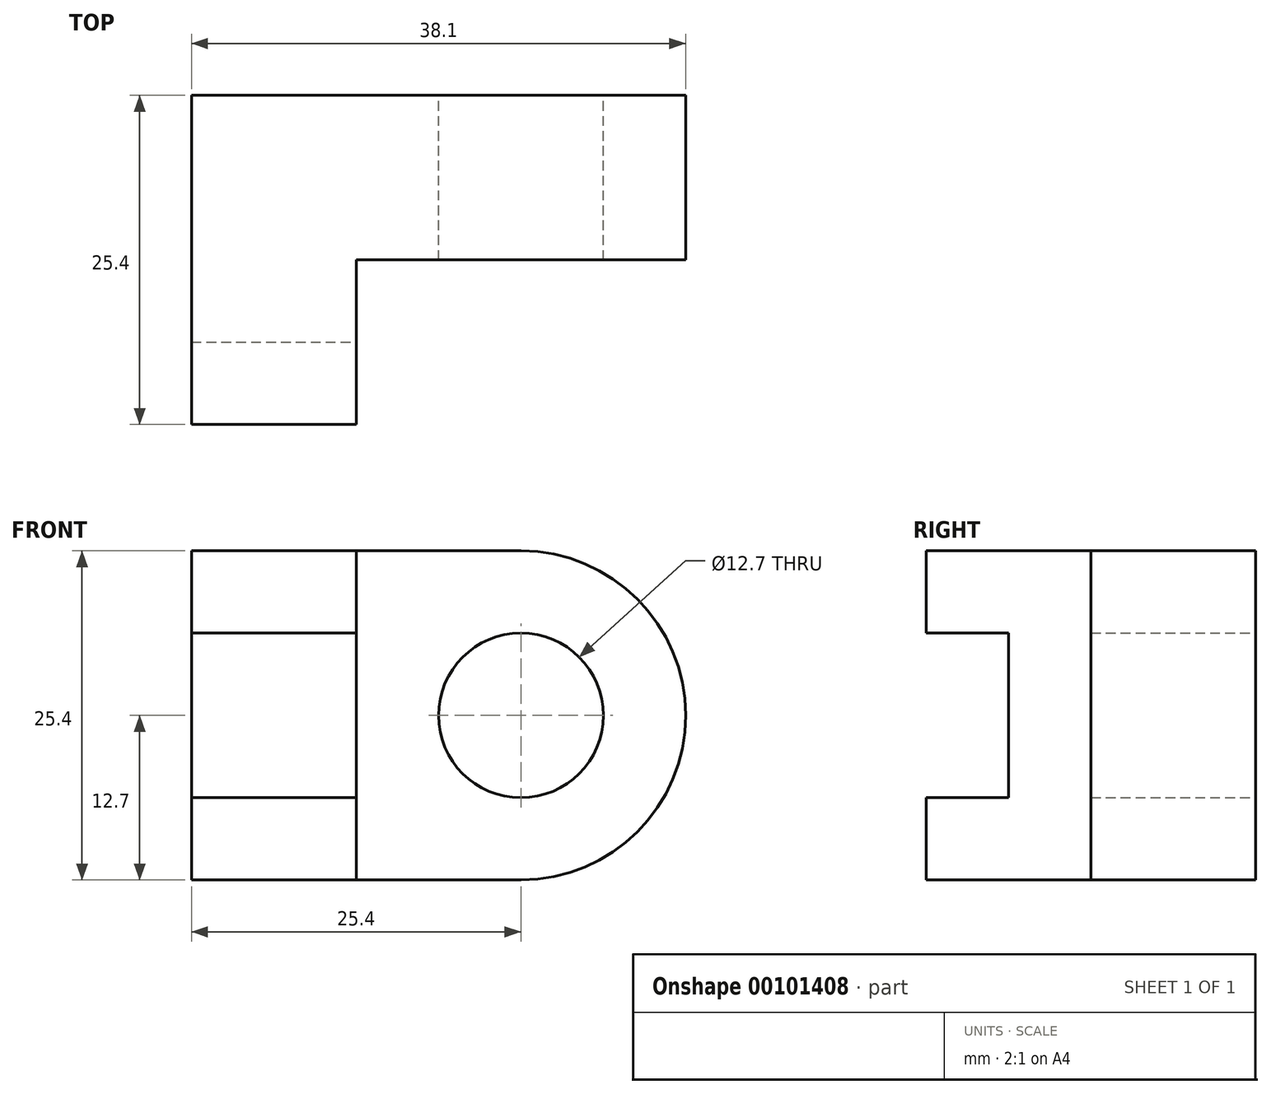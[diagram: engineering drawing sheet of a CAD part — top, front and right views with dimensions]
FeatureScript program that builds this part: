
annotation { "Feature Type Name" : "Feature", "Feature Type Description" : "" }
export const myFeature = defineFeature(function(context is Context, id is Id, definition is map)
    precondition{}
    {
        {
            var Q0;
            Q0=qCreatedBy(makeId("Front.planeOp"),FACE);
            var sketch = newSketch(context, id + "F0", { "sketchPlane" : qUnion([Q0])});
            skLineSegment(sketch, "E0", {"start": v(0, 0) * mm, "end": v(12.7, 0) * mm});
            skLineSegment(sketch, "E1", {"start": v(0, 0) * mm, "end": v(0, 25.4) * mm});
            skLineSegment(sketch, "E2", {"start": v(0, 25.4) * mm, "end": v(12.7, 25.4) * mm});
            skArc(sketch, "E3", {"start": v(12.7, 0) * mm, "mid": v(25.4, 12.7) * mm, "end": v(12.7, 25.4) * mm});
            skCircle(sketch, "E4", {"center": v(12.7, 12.7) * mm, "radius": 6.35 * mm});
            skSolve(sketch);
        }
        {
            var Q0;
            Q0=makeQuery(id+"F0.imprint","IMPRINT",FACE,{"disambiguationData":[TD([[makeQuery(id+"F0.imprint","IMPRINT",EDGE,{"derivedFrom":sQuery(id+"F0.wireOp",EDGE,"E0")}),1.0]])]});
            extrude(context, id + "F1", {"entities" : qUnion([Q0]), "depth" : 12.7 * mm});
        }
        {
            var Q0;
            Q0=qCreatedBy(makeId("Top.planeOp"),FACE);
            var sketch = newSketch(context, id + "F2", { "sketchPlane" : qUnion([Q0])});
            skLineSegment(sketch, "E5", {"start": v(0, 0) * mm, "end": v(0, -25.4) * mm});
            skLineSegment(sketch, "E6", {"start": v(-12.7, -25.4) * mm, "end": v(0, -25.4) * mm});
            skLineSegment(sketch, "E7", {"start": v(-12.7, -25.4) * mm, "end": v(-12.7, 0) * mm});
            skLineSegment(sketch, "E8", {"start": v(0, 0) * mm, "end": v(-12.7, 0) * mm});
            skSolve(sketch);
        }
        {
            var Q0;
            Q0 = qSketchRegion(id + "F2", true);
            extrude(context, id + "F3", {"entities" : qUnion([Q0]), "operationType" : NewBodyOperationType.ADD, "depth" : 25.4 * mm});
        }
        {
            var Q0;
            Q0=makeQuery(id+"F3.opExtrude","SWEPT_FACE",FACE,{"disambiguationData":[OSD([sQuery(id+"F2.wireOp",EDGE,"E6")])]});
            var sketch = newSketch(context, id + "F4", { "sketchPlane" : qUnion([Q0])});
            skLineSegment(sketch, "E9", {"start": v(-12.7, 19.05) * mm, "end": v(0, 19.05) * mm});
            skLineSegment(sketch, "E10", {"start": v(0, 19.05) * mm, "end": v(0, 6.35) * mm});
            skLineSegment(sketch, "E11", {"start": v(0, 6.35) * mm, "end": v(-12.7, 6.35) * mm});
            skLineSegment(sketch, "E12", {"start": v(-12.7, 6.35) * mm, "end": v(-12.7, 19.05) * mm});
            skSolve(sketch);
        }
        {
            var Q0;
            Q0 = qSketchRegion(id + "F4", true);
            extrude(context, id + "F5", {"entities" : qUnion([Q0]), "operationType" : NewBodyOperationType.REMOVE, "oppositeDirection" : true, "depth" : 6.35 * mm});
        }
    });
